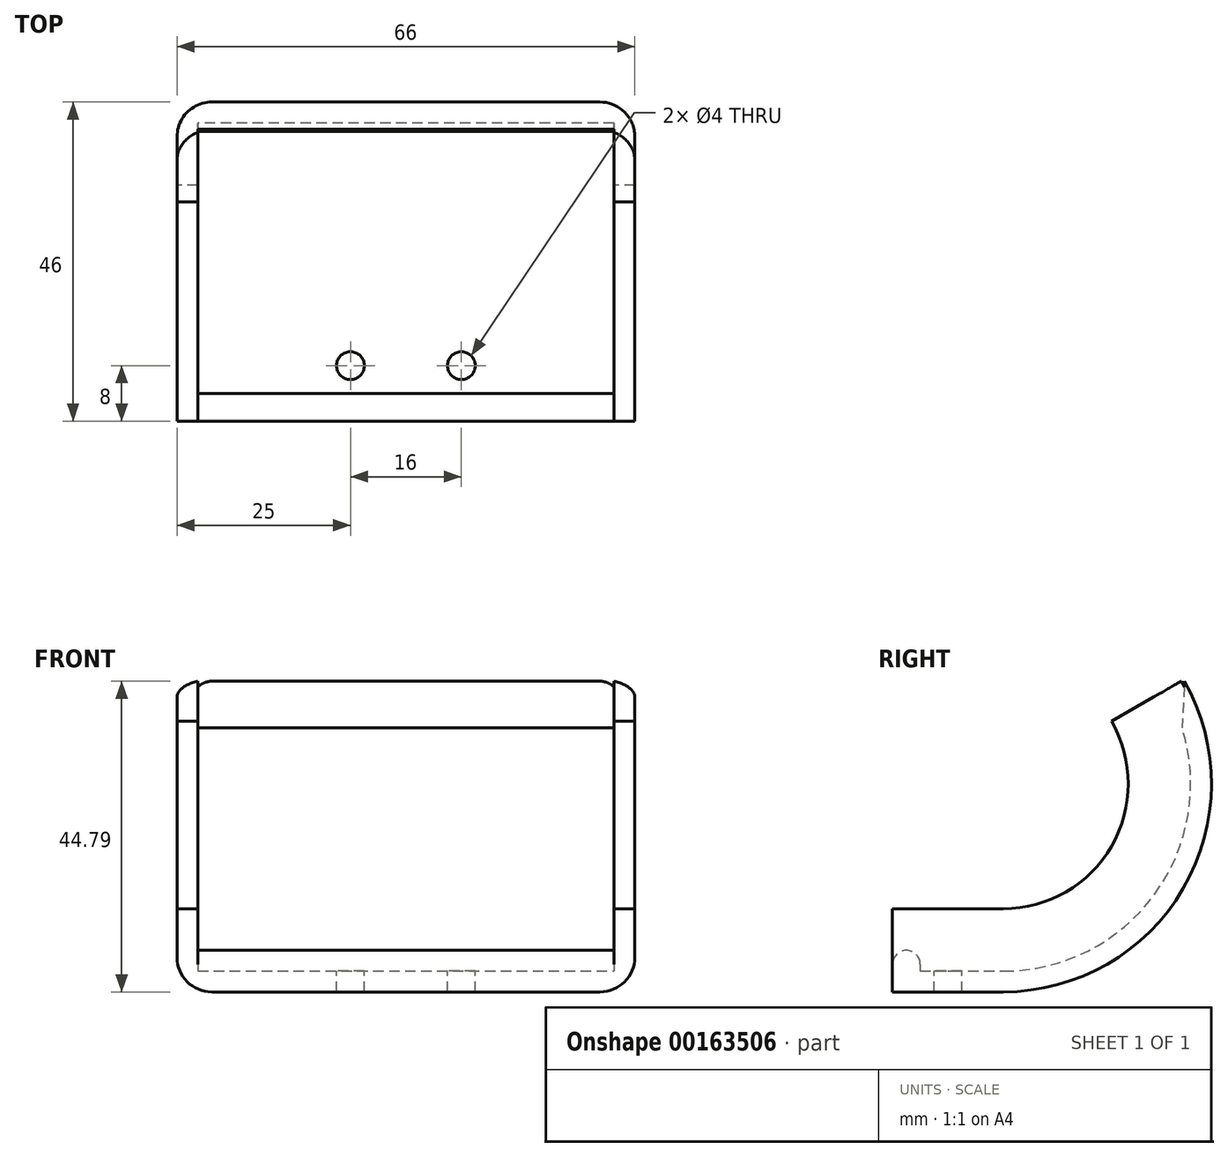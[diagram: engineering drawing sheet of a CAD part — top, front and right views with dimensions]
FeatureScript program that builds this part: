
annotation { "Feature Type Name" : "Feature", "Feature Type Description" : "" }
export const myFeature = defineFeature(function(context is Context, id is Id, definition is map)
    precondition{}
    {
        {
            var Q0;
            Q0=qCreatedBy(makeId("Front.planeOp"),FACE);
            var sketch = newSketch(context, id + "F0", { "sketchPlane" : qUnion([Q0])});
            skLineSegment(sketch, "E0.bottom", {"start": v(-33, 0) * mm, "end": v(33, 0) * mm});
            skLineSegment(sketch, "E0.top", {"start": v(-33, 12) * mm, "end": v(33, 12) * mm});
            skLineSegment(sketch, "E0.left", {"start": v(-33, 0) * mm, "end": v(-33, 12) * mm});
            skLineSegment(sketch, "E0.right", {"start": v(33, 0) * mm, "end": v(33, 12) * mm});
            skLineSegment(sketch, "E1.bottom", {"start": v(-30, 12) * mm, "end": v(30, 12) * mm});
            skLineSegment(sketch, "E1.top", {"start": v(-30, 3) * mm, "end": v(30, 3) * mm});
            skLineSegment(sketch, "E1.left", {"start": v(-30, 12) * mm, "end": v(-30, 3) * mm});
            skLineSegment(sketch, "E1.right", {"start": v(30, 12) * mm, "end": v(30, 3) * mm});
            skLineSegment(sketch, "E2", {"start": v(-37.93, 30) * mm, "end": v(51.96, 30) * mm});
            skSolve(sketch);
        }
        {
            var Q0;
            Q0=makeQuery(id+"F0.imprint","IMPRINT",FACE,{"disambiguationData":[TD([[makeQuery(id+"F0.imprint","IMPRINT",EDGE,{"derivedFrom":sQuery(id+"F0.wireOp",EDGE,"E0.bottom")}),1.0]])]});
            var Q1;
            Q1=sQuery(id+"F0.wireOp",EDGE,"E2");
            revolve(context, id + "F1", {"entities" : qUnion([Q0]), "axis" : qUnion([Q1]), "revolveType" : RevolveType.ONE_DIRECTION, "angle" : 120 * degree});
        }
        {
            var Q0;
            Q0=makeQuery(id+"F1.opRevolve","CAP_EDGE",EDGE,{"disambiguationData":[OSD([sQuery(id+"F0.wireOp",EDGE,"E1.top")])],"isStart":false});
            chamfer(context, id + "F2", {"entities" : qUnion([Q0]), "chamferType" : ChamferType.OFFSET_ANGLE, "width" : 3.9 * mm, "oppositeDirection" : false, "angle" : 60 * degree, "tangentPropagation" : true});
        }
        {
            var Q0;
            Q0=makeQuery(id+"F1.opRevolve","SWEPT_EDGE",EDGE,{"disambiguationData":[OSD([sQuery(id+"F0.wireOp",EDGE,"E0.bottom"),sQuery(id+"F0.wireOp",EDGE,"E0.right")])]});
            var Q1;
            Q1=makeQuery(id+"F1.opRevolve","SWEPT_EDGE",EDGE,{"disambiguationData":[OSD([sQuery(id+"F0.wireOp",EDGE,"E0.bottom"),sQuery(id+"F0.wireOp",EDGE,"E0.left")])]});
            fillet(context, id + "F3", {"entities" : qUnion([Q0, Q1]), "radius" : 5 * mm, "tangentPropagation" : true, "allowEdgeOverflow" : false});
        }
        {
            var Q0;
            Q0=makeQuery(id+"F1.opRevolve","CAP_FACE",FACE,{"disambiguationData":[OSD([sQuery(id+"F0.wireOp",EDGE,"E0.bottom"),sQuery(id+"F0.wireOp",EDGE,"E0.top"),sQuery(id+"F0.wireOp",EDGE,"E0.left"),sQuery(id+"F0.wireOp",EDGE,"E0.right"),sQuery(id+"F0.wireOp",EDGE,"E1.top"),sQuery(id+"F0.wireOp",EDGE,"E1.left"),sQuery(id+"F0.wireOp",EDGE,"E1.right")])],"isStart":true});
            extrude(context, id + "F4", {"entities" : qUnion([Q0]), "operationType" : NewBodyOperationType.ADD, "depth" : 16 * mm});
        }
        {
            var Q0;
            Q0=makeQuery(id+"F4.opExtrude","SWEPT_FACE",FACE,{"disambiguationData":[OSD([sQuery(id+"F0.wireOp",EDGE,"E1.top")])]});
            var sketch = newSketch(context, id + "F5", { "sketchPlane" : qUnion([Q0])});
            skCircle(sketch, "E3", {"center": v(-8, -8) * mm, "radius": 2 * mm});
            skCircle(sketch, "E4.1.0.0", {"center": v(8, -8) * mm, "radius": 2 * mm});
            skLineSegment(sketch, "E4.direction1", {"start": v(-8, -8) * mm, "end": v(8, -8) * mm, "construction": true});
            skLineSegment(sketch, "E5.bottom", {"start": v(-30, -16) * mm, "end": v(30, -16) * mm});
            skLineSegment(sketch, "E5.top", {"start": v(-30, -12) * mm, "end": v(30, -12) * mm});
            skLineSegment(sketch, "E5.left", {"start": v(-30, -16) * mm, "end": v(-30, -12) * mm});
            skLineSegment(sketch, "E5.right", {"start": v(30, -16) * mm, "end": v(30, -12) * mm});
            skSolve(sketch);
        }
        {
            var Q0;
            Q0=makeQuery(id+"F5.imprint","IMPRINT",FACE,{"disambiguationData":[TD([[makeQuery(id+"F5.imprint","IMPRINT",EDGE,{"derivedFrom":sQuery(id+"F5.wireOp",EDGE,"E3")}),1.0]])]});
            var Q1;
            Q1=makeQuery(id+"F5.imprint","IMPRINT",FACE,{"disambiguationData":[TD([[makeQuery(id+"F5.imprint","IMPRINT",EDGE,{"derivedFrom":sQuery(id+"F5.wireOp",EDGE,"E4.1.0.0")}),1.0]])]});
            extrude(context, id + "F6", {"entities" : qUnion([Q0, Q1]), "operationType" : NewBodyOperationType.REMOVE, "endBound" : BoundingType.THROUGH_ALL, "oppositeDirection" : true, "depth" : 25 * mm});
        }
        {
            var Q0;
            Q0=makeQuery(id+"F5.imprint","IMPRINT",FACE,{"disambiguationData":[TD([[makeQuery(id+"F5.imprint","IMPRINT",EDGE,{"derivedFrom":sQuery(id+"F5.wireOp",EDGE,"E5.bottom")}),1.0]])]});
            extrude(context, id + "F7", {"entities" : qUnion([Q0]), "operationType" : NewBodyOperationType.ADD, "depth" : 3 * mm});
        }
        {
            var Q0;
            Q0=makeQuery(id+"F7.opExtrude","CAP_EDGE",EDGE,{"disambiguationData":[OSD([sQuery(id+"F5.wireOp",EDGE,"E5.bottom")])],"isStart":false});
            var Q1;
            Q1=makeQuery(id+"F7.opExtrude","CAP_EDGE",EDGE,{"disambiguationData":[OSD([sQuery(id+"F5.wireOp",EDGE,"E5.top")])],"isStart":false});
            fillet(context, id + "F8", {"entities" : qUnion([Q0, Q1]), "radius" : 2 * mm, "tangentPropagation" : true, "allowEdgeOverflow" : false});
        }
    });
